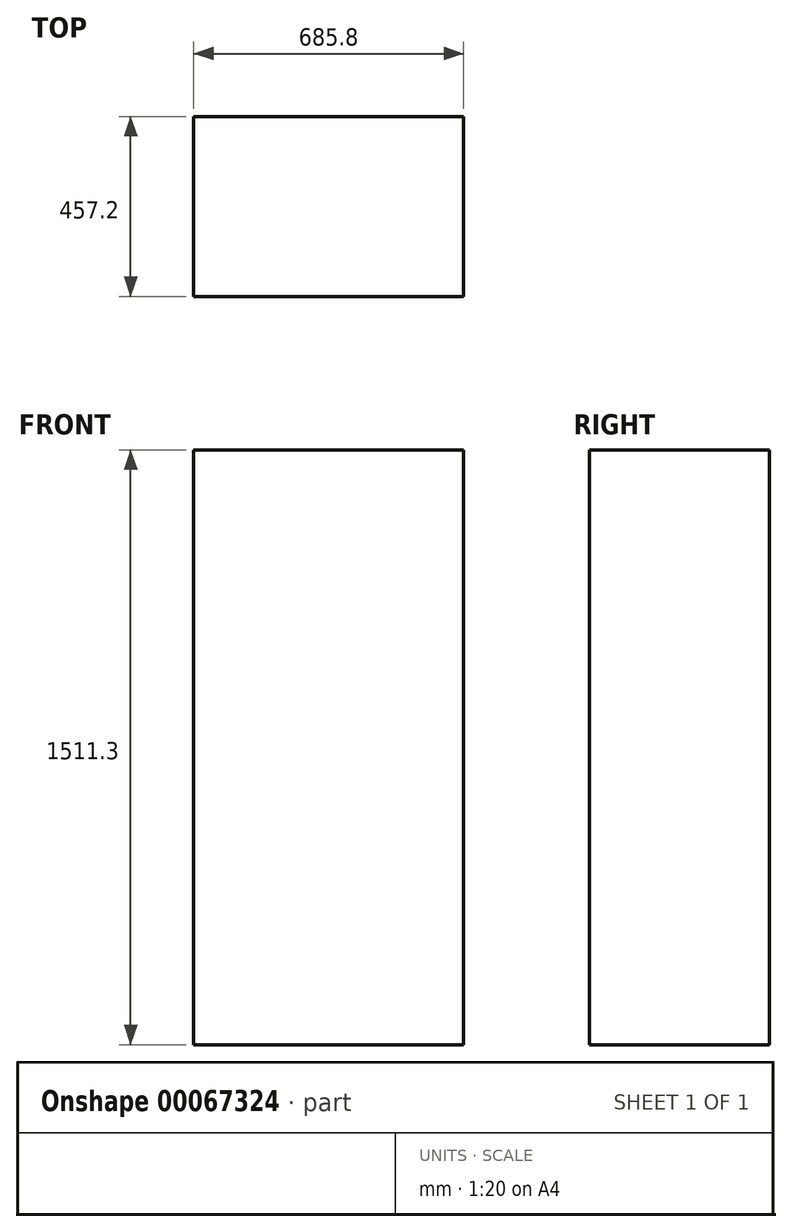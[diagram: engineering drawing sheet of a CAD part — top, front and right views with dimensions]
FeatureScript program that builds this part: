
annotation { "Feature Type Name" : "Feature", "Feature Type Description" : "" }
export const myFeature = defineFeature(function(context is Context, id is Id, definition is map)
    precondition{}
    {
        {
            var Q0;
            Q0=qCreatedBy(makeId("Top.planeOp"),FACE);
            var sketch = newSketch(context, id + "F0", { "sketchPlane" : qUnion([Q0])});
            skLineSegment(sketch, "E0.bottom", {"start": v(-160.92, 277.49) * mm, "end": v(524.88, 277.49) * mm});
            skLineSegment(sketch, "E0.top", {"start": v(-160.92, -179.71) * mm, "end": v(524.88, -179.71) * mm});
            skLineSegment(sketch, "E0.left", {"start": v(-160.92, 277.49) * mm, "end": v(-160.92, -179.71) * mm});
            skLineSegment(sketch, "E0.right", {"start": v(524.88, 277.49) * mm, "end": v(524.88, -179.71) * mm});
            skSolve(sketch);
        }
        {
            var Q0;
            Q0=makeQuery(id+"F0.imprint","IMPRINT",FACE,{"disambiguationData":[TD([[makeQuery(id+"F0.imprint","IMPRINT",EDGE,{"derivedFrom":sQuery(id+"F0.wireOp",EDGE,"E0.bottom")}),-1.0]])]});
            extrude(context, id + "F1", {"entities" : qUnion([Q0]), "depth" : 1511.3 * mm});
        }
    });
